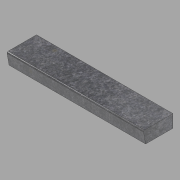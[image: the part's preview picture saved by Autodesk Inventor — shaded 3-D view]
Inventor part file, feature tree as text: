
AUTODESK INVENTOR PART (.ipt)
format: ipt  version: 2022.1 (Build 261234020, 234B)  size: 98,304 bytes
history: native  units: in
note: dims shown in document units (in); Inventor stores cm internally (conversion verified against a paired STEP export)
features: other x3, extrude x1, sketch x1
ambient origin geometry x8: Origin, YZ Plane, XZ Plane, XY Plane, X Axis, Y Axis, Z Axis, Center Point
bodies: Solid1 (feature_tree)
feature tree (5):
  other  "Blocks"
  extrude  "Extrusion1"  Depth=64.875in TaperAngle=0.0deg
  sketch  "Sketch1"  dims[d0=13.0in d1=6.0in d2=13.5in d3=0.5in d4=0.5in d5=64.875in d6=0.0in]
  other  "Profile"
  other  "Profile:1"
